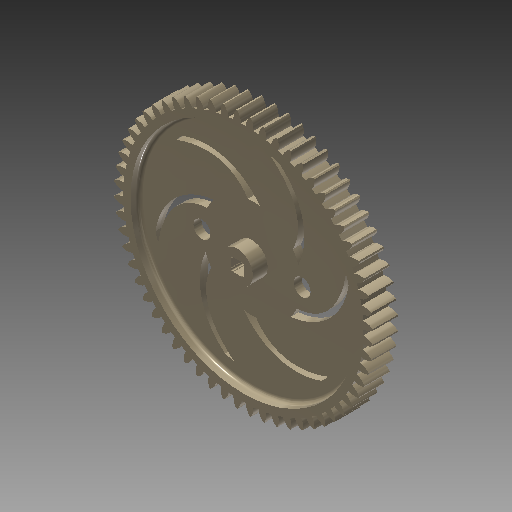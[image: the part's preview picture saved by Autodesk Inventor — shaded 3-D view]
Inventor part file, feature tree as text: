
AUTODESK INVENTOR PART (.ipt)
format: ipt  version: 2018 (Build 220112000, 112)  size: 1,127,424 bytes
history: native  units: mm (DEFAULTED — no unit token found)
features: imported_body x1, sketch x1, other x1, extrude x1
ambient origin geometry x8: Origin, YZ Plane, XZ Plane, XY Plane, X Axis, Y Axis, Z Axis, Center Point
bodies: Solid1 (feature_tree)
feature tree (4):
  imported_body  "Base1"
  sketch  "Sketch1"  dims[d1=8.001mm d5=25.4mm d6=0.0mm d7=0.0mm d8=0.0mm]
  other  "Srf1"
  extrude  "ExtrusionSrf1"  Depth=25.4mm TaperAngle=0.0deg
